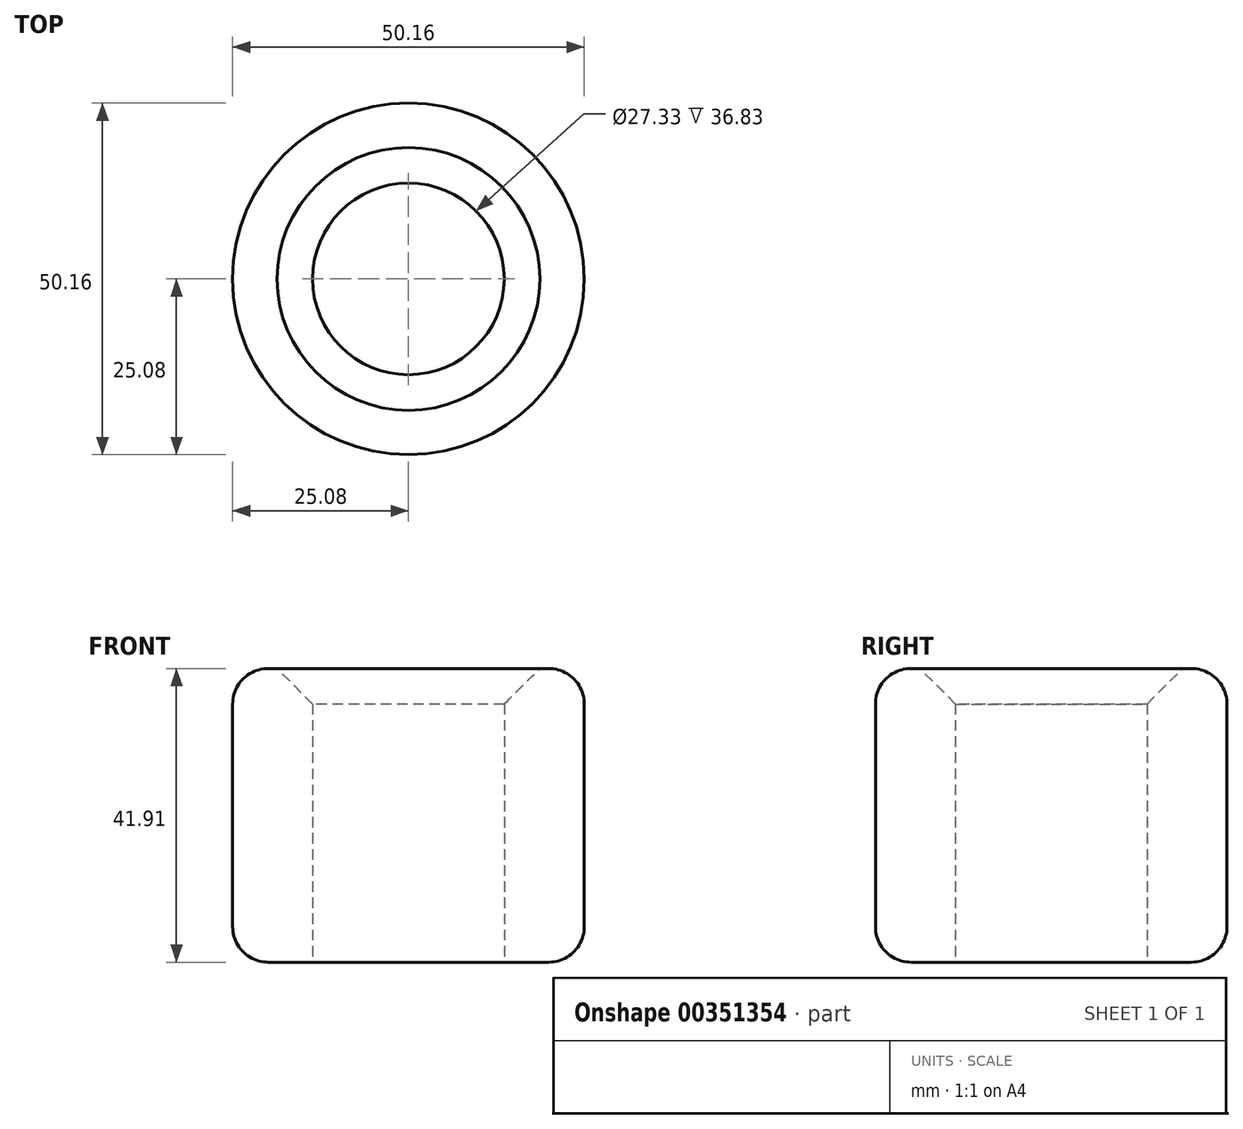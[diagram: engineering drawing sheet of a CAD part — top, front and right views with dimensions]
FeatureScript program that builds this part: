
annotation { "Feature Type Name" : "Feature", "Feature Type Description" : "" }
export const myFeature = defineFeature(function(context is Context, id is Id, definition is map)
    precondition{}
    {
        {
            var Q0;
            Q0=qCreatedBy(makeId("Top.planeOp"),FACE);
            var sketch = newSketch(context, id + "F0", { "sketchPlane" : qUnion([Q0])});
            skCircle(sketch, "E0", {"center": v(0, 0) * mm, "radius": 25.08 * mm});
            skCircle(sketch, "E1", {"center": v(0, 0) * mm, "radius": 13.67 * mm});
            skSolve(sketch);
        }
        {
            var Q0;
            Q0 = qSketchRegion(id + "F0", true);
            extrude(context, id + "F1", {"entities" : qUnion([Q0]), "depth" : 41.9 * mm});
        }
        {
            var Q0;
            Q0=makeQuery(id+"F1.opExtrude","CAP_EDGE",EDGE,{"disambiguationData":[OSD([sQuery(id+"F0.wireOp",EDGE,"E1")])],"isStart":false});
            chamfer(context, id + "F2", {"entities" : qUnion([Q0]), "width" : 5.08 * mm, "tangentPropagation" : true});
        }
        {
            var Q0;
            Q0=makeQuery(id+"F1.opExtrude","CAP_EDGE",EDGE,{"disambiguationData":[OSD([sQuery(id+"F0.wireOp",EDGE,"E0")])],"isStart":false});
            var Q1;
            Q1=makeQuery(id+"F1.opExtrude","CAP_EDGE",EDGE,{"disambiguationData":[OSD([sQuery(id+"F0.wireOp",EDGE,"E0")])],"isStart":true});
            fillet(context, id + "F3", {"entities" : qUnion([Q0, Q1]), "radius" : 5.08 * mm, "tangentPropagation" : true, "allowEdgeOverflow" : false});
        }
    });
